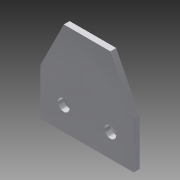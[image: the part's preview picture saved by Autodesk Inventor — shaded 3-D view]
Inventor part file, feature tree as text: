
AUTODESK INVENTOR PART (.ipt)
format: ipt  version: 2015 SP1 (Build 190203100, 203)  size: 115,712 bytes
history: native  units: in
note: dims shown in document units (in); Inventor stores cm internally (conversion verified against a paired STEP export)
features: sketch x3, extrude x2, hole x1, projected_geometry x1
ambient origin geometry x8: Origin, YZ Plane, XZ Plane, XY Plane, X Axis, Y Axis, Z Axis, Center Point
bodies: Solid1 (feature_tree)
feature tree (7):
  extrude  "Extrusion1"  Depth=2.0in
  hole  "Hole1"  [1 undecoded]
  extrude  "Extrusion2"  Depth=1.0in
  sketch  "Sketch1"  dims[d0=2.0in d1=2.0in]
  sketch  "Sketch2"  dims[d2=0.125in d3=0.0in d4=0.5in]
  projected_geometry  "Projected Loop1"
  sketch  "Sketch3"  dims[d5=0.5in d6=0.5in d7=0.5in d8=0.25in d9=0.75in d10=0.375in d11=0.25in d12=0.5635in d13=1.0in d14=0.8108in d19=1.0in d20=1.0in d21=1.0in d22=0.5in d23=1.0in d24=0.0in]
note: 1 required parameter value undecoded (feature->parameter linkage not recoverable at this tier; creation-order binding heuristic only, values carry confidence <= 0.55)
